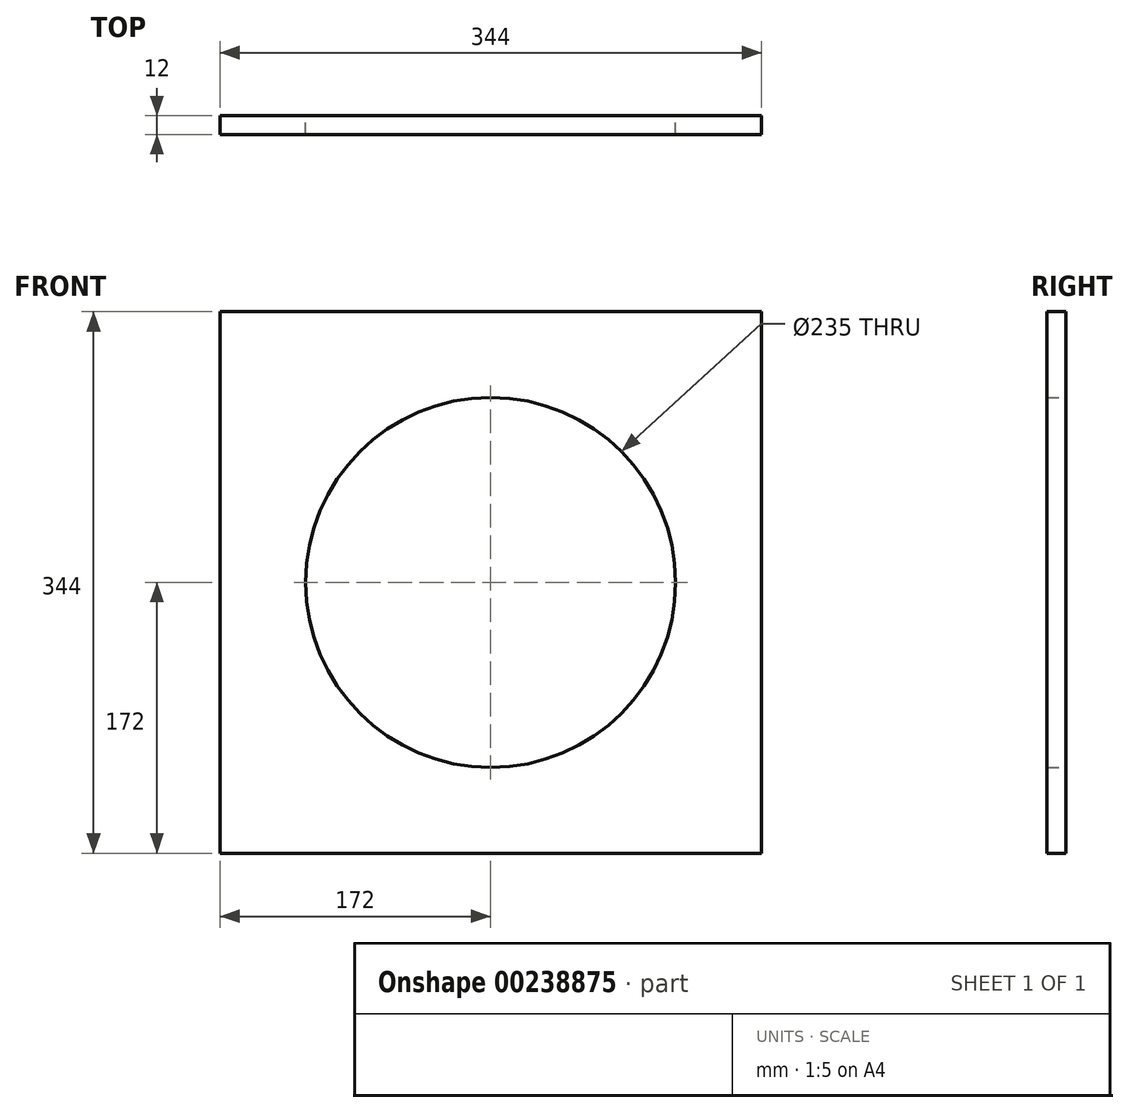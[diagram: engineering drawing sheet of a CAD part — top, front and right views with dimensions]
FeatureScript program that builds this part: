
annotation { "Feature Type Name" : "Feature", "Feature Type Description" : "" }
export const myFeature = defineFeature(function(context is Context, id is Id, definition is map)
    precondition{}
    {
        {
            var Q0;
            Q0=qCreatedBy(makeId("Front.planeOp"), FACE);
            var sketch = newSketch(context, id + "F0", { "sketchPlane" : qUnion([Q0])});
            skLineSegment(sketch, "E0.bottom", {"start": v(0, 0) * mm, "end": v(344, 0) * mm});
            skLineSegment(sketch, "E0.top", {"start": v(0, 344) * mm, "end": v(344, 344) * mm});
            skLineSegment(sketch, "E0.left", {"start": v(0, 0) * mm, "end": v(0, 344) * mm});
            skLineSegment(sketch, "E0.right", {"start": v(344, 0) * mm, "end": v(344, 344) * mm});
            skCircle(sketch, "E1", {"center": v(172, 172) * mm, "radius": 117.5 * mm});
            skSolve(sketch);
        }
        {
            var Q0;
            Q0 = qSketchRegion(id + "F0", true);
            extrude(context, id + "F1", {"entities" : qUnion([Q0]), "depth" : 12 * mm, "offsetDistance" : 25 * mm});
        }
    });
